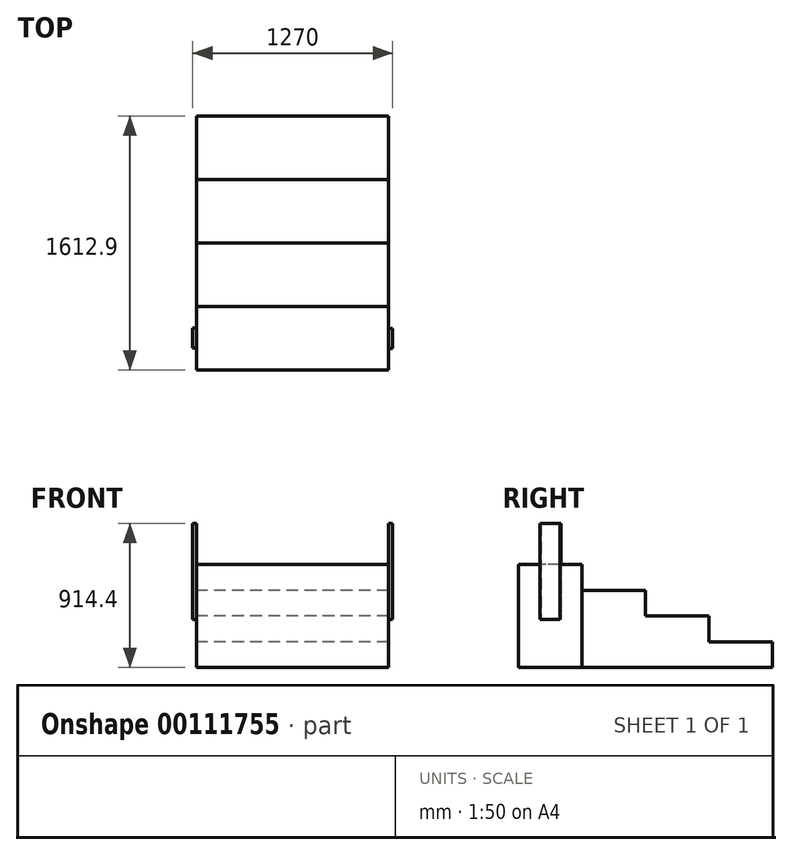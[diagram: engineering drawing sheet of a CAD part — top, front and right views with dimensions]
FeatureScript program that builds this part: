
annotation { "Feature Type Name" : "Feature", "Feature Type Description" : "" }
export const myFeature = defineFeature(function(context is Context, id is Id, definition is map)
    precondition{}
    {
        {
            var Q0;
            Q0=qCreatedBy(makeId("Front.planeOp"),FACE);
            var sketch = newSketch(context, id + "F0", { "sketchPlane" : qUnion([Q0])});
            skLineSegment(sketch, "E0.bottom", {"start": v(-57.55, 608.76) * mm, "end": v(1161.65, 608.76) * mm});
            skLineSegment(sketch, "E0.top", {"start": v(-57.55, -45.3) * mm, "end": v(1161.65, -45.3) * mm});
            skLineSegment(sketch, "E0.left", {"start": v(-57.55, 608.76) * mm, "end": v(-57.55, -45.3) * mm});
            skLineSegment(sketch, "E0.right", {"start": v(1161.65, 608.76) * mm, "end": v(1161.65, -45.3) * mm});
            skSolve(sketch);
        }
        {
            var Q0;
            Q0 = qSketchRegion(id + "F0", true);
            extrude(context, id + "F1", {"entities" : qUnion([Q0]), "oppositeDirection" : true, "depth" : 403.22 * mm});
        }
        {
            var Q0;
            Q0=makeQuery(id+"F1.opExtrude","CAP_FACE",FACE,{"disambiguationData":[OSD([sQuery(id+"F0.wireOp",EDGE,"E0.bottom"),sQuery(id+"F0.wireOp",EDGE,"E0.top"),sQuery(id+"F0.wireOp",EDGE,"E0.left"),sQuery(id+"F0.wireOp",EDGE,"E0.right")])],"isStart":false});
            var sketch = newSketch(context, id + "F2", { "sketchPlane" : qUnion([Q0])});
            skLineSegment(sketch, "E1.bottom", {"start": v(-1161.65, 445.24) * mm, "end": v(57.55, 445.24) * mm});
            skLineSegment(sketch, "E1.top", {"start": v(-1161.65, -45.3) * mm, "end": v(57.55, -45.3) * mm});
            skLineSegment(sketch, "E1.left", {"start": v(-1161.65, 445.24) * mm, "end": v(-1161.65, -45.3) * mm});
            skLineSegment(sketch, "E1.right", {"start": v(57.55, 445.24) * mm, "end": v(57.55, -45.3) * mm});
            skSolve(sketch);
        }
        {
            var Q0;
            Q0=makeQuery(id+"F2.imprint","IMPRINT",FACE,{"disambiguationData":[TD([[makeQuery(id+"F2.imprint","IMPRINT",EDGE,{"derivedFrom":sQuery(id+"F2.wireOp",EDGE,"E1.bottom")}),-1.0]])]});
            extrude(context, id + "F3", {"entities" : qUnion([Q0]), "depth" : 403.22 * mm});
        }
        {
            var Q0;
            Q0=makeQuery(id+"F3.opExtrude","CAP_FACE",FACE,{"disambiguationData":[OSD([sQuery(id+"F2.wireOp",EDGE,"E1.bottom"),sQuery(id+"F2.wireOp",EDGE,"E1.top"),sQuery(id+"F2.wireOp",EDGE,"E1.left"),sQuery(id+"F2.wireOp",EDGE,"E1.right")])],"isStart":false});
            var sketch = newSketch(context, id + "F4", { "sketchPlane" : qUnion([Q0])});
            skLineSegment(sketch, "E2.bottom", {"start": v(-1161.65, 281.73) * mm, "end": v(57.55, 281.73) * mm});
            skLineSegment(sketch, "E2.top", {"start": v(-1161.65, -45.3) * mm, "end": v(57.55, -45.3) * mm});
            skLineSegment(sketch, "E2.left", {"start": v(-1161.65, 281.73) * mm, "end": v(-1161.65, -45.3) * mm});
            skLineSegment(sketch, "E2.right", {"start": v(57.55, 281.73) * mm, "end": v(57.55, -45.3) * mm});
            skSolve(sketch);
        }
        {
            var Q0;
            Q0=makeQuery(id+"F4.imprint","IMPRINT",FACE,{"disambiguationData":[TD([[makeQuery(id+"F4.imprint","IMPRINT",EDGE,{"derivedFrom":sQuery(id+"F4.wireOp",EDGE,"E2.bottom")}),-1.0]])]});
            extrude(context, id + "F5", {"entities" : qUnion([Q0]), "operationType" : NewBodyOperationType.ADD, "depth" : 403.22 * mm});
        }
        {
            var Q0;
            Q0=makeQuery(id+"F5.opExtrude","CAP_FACE",FACE,{"disambiguationData":[OSD([sQuery(id+"F4.wireOp",EDGE,"E2.bottom"),sQuery(id+"F4.wireOp",EDGE,"E2.top"),sQuery(id+"F4.wireOp",EDGE,"E2.left"),sQuery(id+"F4.wireOp",EDGE,"E2.right")])],"isStart":false});
            var sketch = newSketch(context, id + "F6", { "sketchPlane" : qUnion([Q0])});
            skLineSegment(sketch, "E3.bottom", {"start": v(-1161.65, 118.22) * mm, "end": v(57.55, 118.22) * mm});
            skLineSegment(sketch, "E3.top", {"start": v(-1161.65, -45.3) * mm, "end": v(57.55, -45.3) * mm});
            skLineSegment(sketch, "E3.left", {"start": v(-1161.65, 118.22) * mm, "end": v(-1161.65, -45.3) * mm});
            skLineSegment(sketch, "E3.right", {"start": v(57.55, 118.22) * mm, "end": v(57.55, -45.3) * mm});
            skSolve(sketch);
        }
        {
            var Q0;
            Q0=makeQuery(id+"F6.imprint","IMPRINT",FACE,{"disambiguationData":[TD([[makeQuery(id+"F6.imprint","IMPRINT",EDGE,{"derivedFrom":sQuery(id+"F6.wireOp",EDGE,"E3.bottom")}),-1.0]])]});
            extrude(context, id + "F7", {"entities" : qUnion([Q0]), "operationType" : NewBodyOperationType.ADD, "depth" : 403.22 * mm});
        }
        {
            var Q0;
            Q0=makeQuery(id+"F1.opExtrude","SWEPT_FACE",FACE,{"disambiguationData":[OSD([sQuery(id+"F0.wireOp",EDGE,"E0.right")])]});
            var sketch = newSketch(context, id + "F8", { "sketchPlane" : qUnion([Q0])});
            skLineSegment(sketch, "E4.bottom", {"start": v(135.3, 869.1) * mm, "end": v(262.3, 869.1) * mm});
            skLineSegment(sketch, "E4.top", {"start": v(135.3, 259.5) * mm, "end": v(262.3, 259.5) * mm});
            skLineSegment(sketch, "E4.left", {"start": v(135.3, 869.1) * mm, "end": v(135.3, 259.5) * mm});
            skLineSegment(sketch, "E4.right", {"start": v(262.3, 869.1) * mm, "end": v(262.3, 259.5) * mm});
            skSolve(sketch);
        }
        {
            var Q0;
            {var subQ0=sQuery(id+"F8.wireOp",EDGE,"E4.bottom");Q0=makeQuery(id+"F8.imprint","IMPRINT",FACE,{"disambiguationData":[TD([[makeQuery(id+"F8.imprint","IMPRINT",EDGE,{"derivedFrom":subQ0}),-1.0]])]});}
            var Q1;
            {var subQ0=sQuery(id+"F8.wireOp",EDGE,"E4.top");Q1=makeQuery(id+"F8.imprint","IMPRINT",FACE,{"disambiguationData":[TD([[makeQuery(id+"F8.imprint","IMPRINT",EDGE,{"derivedFrom":subQ0}),1.0]])]});}
            extrude(context, id + "F9", {"entities" : qUnion([Q0, Q1]), "depth" : 25.4 * mm});
        }
        {
            var Q0;
            Q0=makeQuery(id+"F1.opExtrude","SWEPT_FACE",FACE,{"disambiguationData":[OSD([sQuery(id+"F0.wireOp",EDGE,"E0.left")])]});
            var sketch = newSketch(context, id + "F10", { "sketchPlane" : qUnion([Q0])});
            skLineSegment(sketch, "E5.bottom", {"start": v(-266.88, 869.1) * mm, "end": v(-139.88, 869.1) * mm});
            skLineSegment(sketch, "E5.top", {"start": v(-266.88, 259.5) * mm, "end": v(-139.88, 259.5) * mm});
            skLineSegment(sketch, "E5.left", {"start": v(-266.88, 869.1) * mm, "end": v(-266.88, 259.5) * mm});
            skLineSegment(sketch, "E5.right", {"start": v(-139.88, 869.1) * mm, "end": v(-139.88, 259.5) * mm});
            skSolve(sketch);
        }
        {
            var Q0;
            {var subQ0=sQuery(id+"F10.wireOp",EDGE,"E5.top");Q0=makeQuery(id+"F10.imprint","IMPRINT",FACE,{"disambiguationData":[TD([[makeQuery(id+"F10.imprint","IMPRINT",EDGE,{"derivedFrom":subQ0}),1.0]])]});}
            var Q1;
            {var subQ0=sQuery(id+"F10.wireOp",EDGE,"E5.bottom");Q1=makeQuery(id+"F10.imprint","IMPRINT",FACE,{"disambiguationData":[TD([[makeQuery(id+"F10.imprint","IMPRINT",EDGE,{"derivedFrom":subQ0}),-1.0]])]});}
            extrude(context, id + "F11", {"entities" : qUnion([Q0, Q1]), "depth" : 25.4 * mm});
        }
    });
